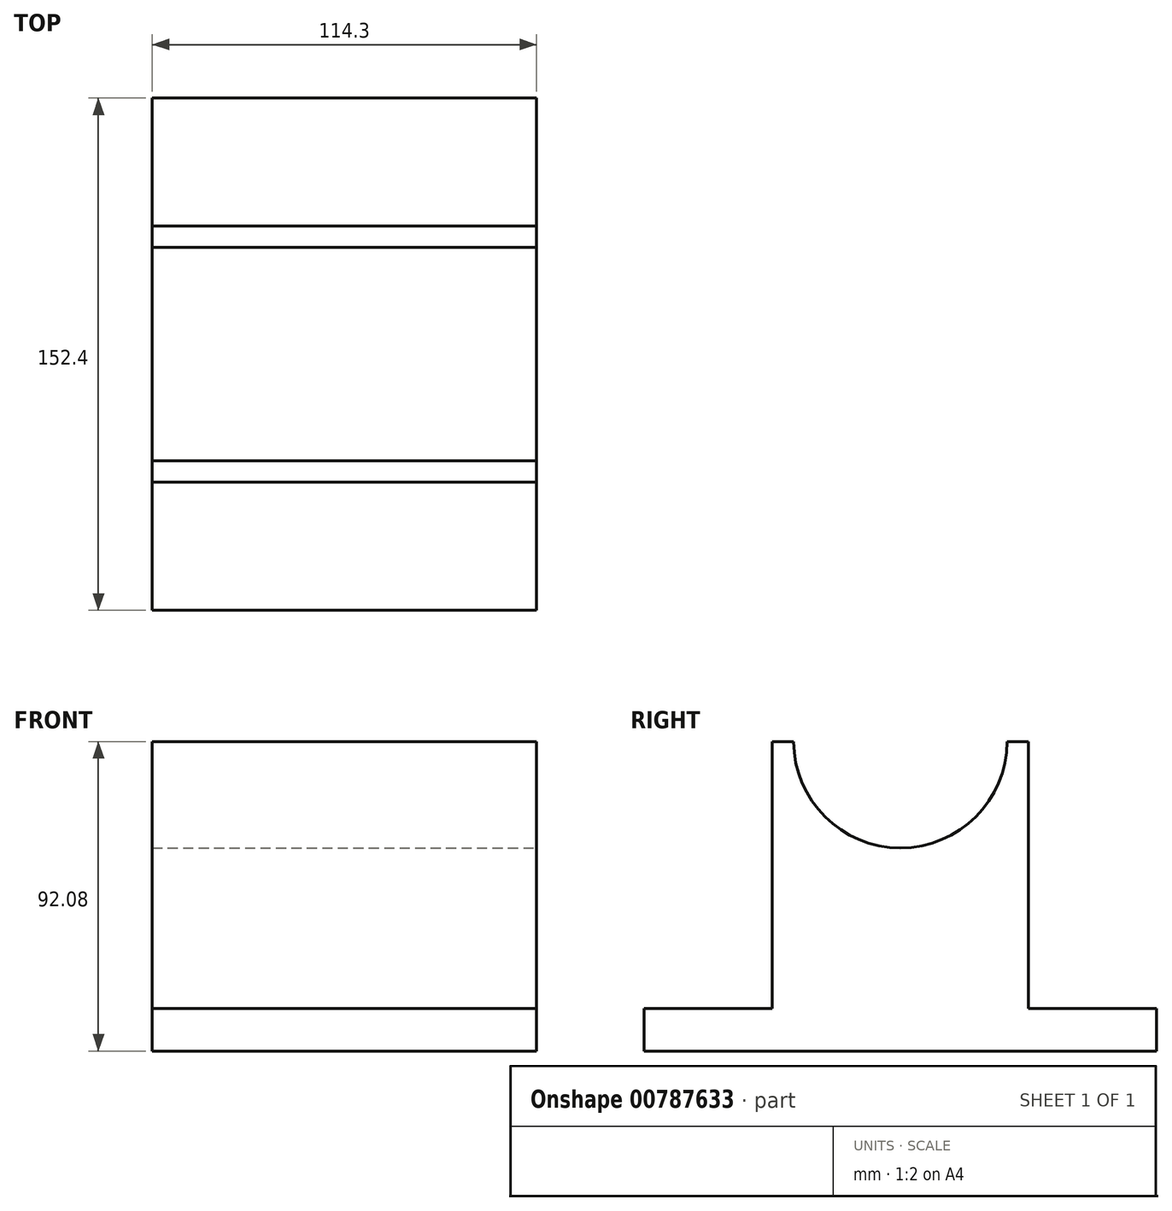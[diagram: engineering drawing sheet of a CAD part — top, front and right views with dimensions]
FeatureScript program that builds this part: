
annotation { "Feature Type Name" : "Feature", "Feature Type Description" : "" }
export const myFeature = defineFeature(function(context is Context, id is Id, definition is map)
    precondition{}
    {
        {
            var Q0;
            Q0=qCreatedBy(makeId("Right.planeOp"),FACE);
            var sketch = newSketch(context, id + "F0", { "sketchPlane" : qUnion([Q0])});
            skLineSegment(sketch, "E0", {"start": v(0, 0) * mm, "end": v(152.4, 0) * mm});
            skLineSegment(sketch, "E1", {"start": v(152.4, 0) * mm, "end": v(152.4, 12.7) * mm});
            skLineSegment(sketch, "E2", {"start": v(152.4, 12.7) * mm, "end": v(114.3, 12.7) * mm});
            skLineSegment(sketch, "E3", {"start": v(114.3, 12.7) * mm, "end": v(114.3, 92.08) * mm});
            skLineSegment(sketch, "E4", {"start": v(114.3, 92.08) * mm, "end": v(114.3, 12.7) * mm});
            skLineSegment(sketch, "E5", {"start": v(114.3, 92.08) * mm, "end": v(38.1, 92.08) * mm});
            skLineSegment(sketch, "E6", {"start": v(38.1, 92.08) * mm, "end": v(38.1, 12.7) * mm});
            skLineSegment(sketch, "E7", {"start": v(38.1, 12.7) * mm, "end": v(0, 12.7) * mm});
            skLineSegment(sketch, "E8", {"start": v(0, 12.7) * mm, "end": v(0, 0) * mm});
            skLineSegment(sketch, "E9", {"start": v(239.73, -49.4) * mm, "end": v(219.46, -67.99) * mm});
            skSolve(sketch);
        }
        {
            var Q0;
            Q0 = qSketchRegion(id + "F0", true);
            extrude(context, id + "F1", {"entities" : qUnion([Q0]), "depth" : 114.3 * mm, "offsetDistance" : 25.4 * mm});
        }
        {
            var Q0;
            Q0=makeQuery(id+"F1.opExtrude","CAP_FACE",FACE,{"disambiguationData":[OSD([sQuery(id+"F0.wireOp",EDGE,"E0"),sQuery(id+"F0.wireOp",EDGE,"E1"),sQuery(id+"F0.wireOp",EDGE,"E2"),sQuery(id+"F0.wireOp",EDGE,"E4"),sQuery(id+"F0.wireOp",EDGE,"E5"),sQuery(id+"F0.wireOp",EDGE,"E6"),sQuery(id+"F0.wireOp",EDGE,"E7"),sQuery(id+"F0.wireOp",EDGE,"E8")])],"isStart":false});
            var sketch = newSketch(context, id + "F2", { "sketchPlane" : qUnion([Q0])});
            skLineSegment(sketch, "E10", {"start": v(76.2, 92.08) * mm, "end": v(107.95, 92.08) * mm});
            skLineSegment(sketch, "E11", {"start": v(76.2, 92.08) * mm, "end": v(44.45, 92.08) * mm});
            skSolve(sketch);
        }
        {
            var Q0;
            {var subQ2=sQuery(id+"F2.wireOp",EDGE,"E10");Q0=makeQuery(id+"F2.imprint","IMPRINT",FACE,{"disambiguationData":[TD([[makeQuery(id+"F2.imprint","IMPRINT",EDGE,{"derivedFrom":subQ2}),1.0]])]});}
            var sketch = newSketch(context, id + "F3", { "sketchPlane" : qUnion([Q0])});
            skCircle(sketch, "E12", {"center": v(76.2, 92.17) * mm, "radius": 31.75 * mm});
            skSolve(sketch);
        }
        {
            var Q0;
            Q0 = qSketchRegion(id + "F3", true);
            extrude(context, id + "F4", {"entities" : qUnion([Q0]), "operationType" : NewBodyOperationType.REMOVE, "endBound" : BoundingType.THROUGH_ALL, "oppositeDirection" : true, "depth" : 25.4 * mm, "offsetDistance" : 25.4 * mm});
        }
    });
